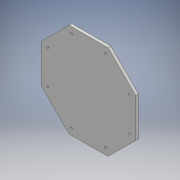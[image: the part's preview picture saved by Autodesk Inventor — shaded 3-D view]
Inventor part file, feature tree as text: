
AUTODESK INVENTOR PART (.ipt)
format: ipt  version: 2017 (Build 210142000, 142)  size: 125,952 bytes
history: native  units: mm
features: plane x1, extrude x1, chamfer x1, sketch x1, projected_geometry x1
ambient origin geometry x8: Origin, YZ Plane, XZ Plane, XY Plane, X Axis, Y Axis, Z Axis, Center Point
bodies: Solid1 (feature_tree)
feature tree (5):
  plane  "Work Plane13"
  extrude  "Extrusion11"  Depth=5.0mm TaperAngle=45.0deg
  chamfer  "Chamfer2"  [1 undecoded]
  sketch  "Sketch13"  dims[d52=5.0mm d53=0.0mm d57=1.0mm d58=2.0mm d59=45.0deg]
  projected_geometry  "Projected Loop11"
note: 1 required parameter value undecoded (feature->parameter linkage not recoverable at this tier; creation-order binding heuristic only, values carry confidence <= 0.55)
